# Revit family: Gira_264803
name_source: partatom
category: Allgemeines Modell
revit_build: Autodesk Revit 2017 (Build: 20160225_1515(x64)
units: mm (PartAtom-declared; Revit-internal decimal feet)

## family parameters
Basisbauteil = Fläche
Beim Laden mit Abzugskörper schneiden = Nein
Bemaßung runder Anschluss = Durchmesser verwenden
Gemeinsam genutzt = Nein
Kann Basisbauteil für Bewehrung sein = Nein
Raumberechnungspunkt = Nein
Teiletyp = Normal

## types (1)
- Gira_264803
    Ausführung der Oberfläche = nicht zutreffend
    BIM = https://media.stage.bim.site
    Befestigungsart = sonstige
    Beschreibung = Montagerahmen  Reinweiß glänzend
    Beschriftungsfeld = ohne Beschriftungsfeld
    Datenblatt = https://katalog.gira.de
    Farbe = weiß
    GTIN = 4010337463511
    Geeignet für Schutzart (IP) = IP20
    HAN = 264803
    Halogenfrei = Ja
    Hersteller = Gira
    Lüsterklemme = Nein
    Mit Aufdruck = Nein
    Mit Klappdeckel = Nein
    Mit Staubschutz = Nein
    Mit Zugentlastung = Nein
    Montageart = sonstige
    Oberfläche = sonstige
    Produktseite = http://katalog.gira.de
    RAL-Nummer (ähnlich) = 9010
    Tragring = Nein
    Transparent = Nein
    Typname = Montagerahmen System 55 Reinweiß
    URL = https://www.gira.de
    Verwendung = sonstige
    Vorgabe-Ansicht = 1219 mm
    Werkstoff = sonstige
    Werkstoffgüte = sonstige
    Zusammenstellung = Zentralplatte

## geometry (parser evidence)
native form markers: Sweep x2
no freeform markers — native parametric forms only
